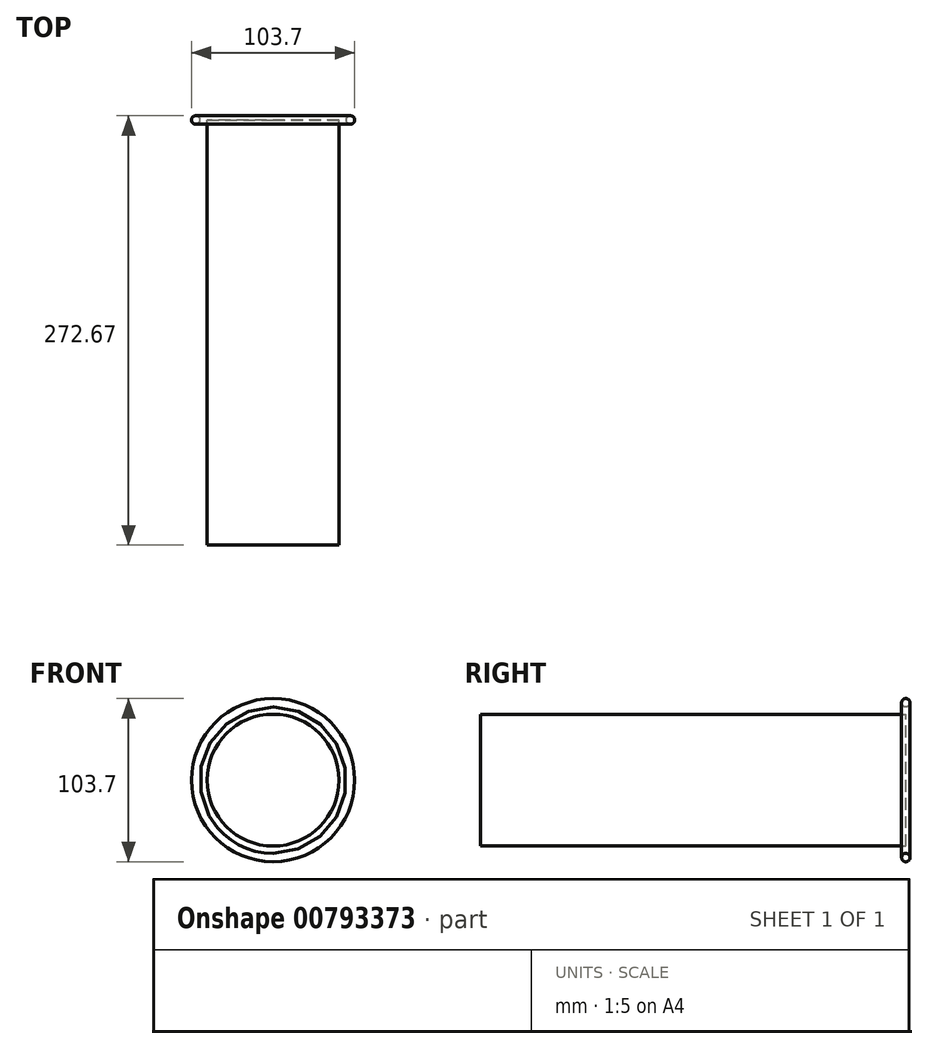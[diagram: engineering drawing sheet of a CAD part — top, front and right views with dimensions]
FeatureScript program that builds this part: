
annotation { "Feature Type Name" : "Feature", "Feature Type Description" : "" }
export const myFeature = defineFeature(function(context is Context, id is Id, definition is map)
    precondition{}
    {
        {
            var Q0;
            Q0=qCreatedBy(makeId("Front.planeOp"),FACE);
            var sketch = newSketch(context, id + "F0", { "sketchPlane" : qUnion([Q0])});
            skCircle(sketch, "E0", {"center": v(0, 0) * mm, "radius": 41.9 * mm});
            skSolve(sketch);
        }
        {
            var Q0;
            Q0=makeQuery(id+"F0.imprint","IMPRINT",FACE,{"disambiguationData":[TD([[makeQuery(id+"F0.imprint","IMPRINT",EDGE,{"derivedFrom":sQuery(id+"F0.wireOp",EDGE,"E0")}),1.0]])]});
            extrude(context, id + "F1", {"entities" : qUnion([Q0]), "depth" : 270 * mm, "offsetDistance" : 25 * mm});
        }
        {
            var Q0;
            Q0=qCreatedBy(makeId("Right.planeOp"),FACE);
            var sketch = newSketch(context, id + "F2", { "sketchPlane" : qUnion([Q0])});
            skLineSegment(sketch, "E1", {"start": v(0, 0) * mm, "end": v(0, 49.18) * mm});
            skCircle(sketch, "E2", {"center": v(0, 49.18) * mm, "radius": 2.67 * mm});
            skLineSegment(sketch, "E3", {"start": v(0, 0) * mm, "end": v(21.81, 0) * mm});
            skSolve(sketch);
        }
        {
            var Q0;
            Q0=makeQuery(id+"F2.imprint","IMPRINT",FACE,{"disambiguationData":[TD([[makeQuery(id+"F2.imprint","IMPRINT",EDGE,{"derivedFrom":sQuery(id+"F2.wireOp",EDGE,"E2")}),1.0]])]});
            var Q1;
            Q1=sQuery(id+"F2.wireOp",EDGE,"E3");
            revolve(context, id + "F3", {"surfaceOperationType" : NewSurfaceOperationType.NEW, "entities" : qUnion([Q0]), "axis" : qUnion([Q1]), "revolveType" : RevolveType.FULL});
        }
    });
